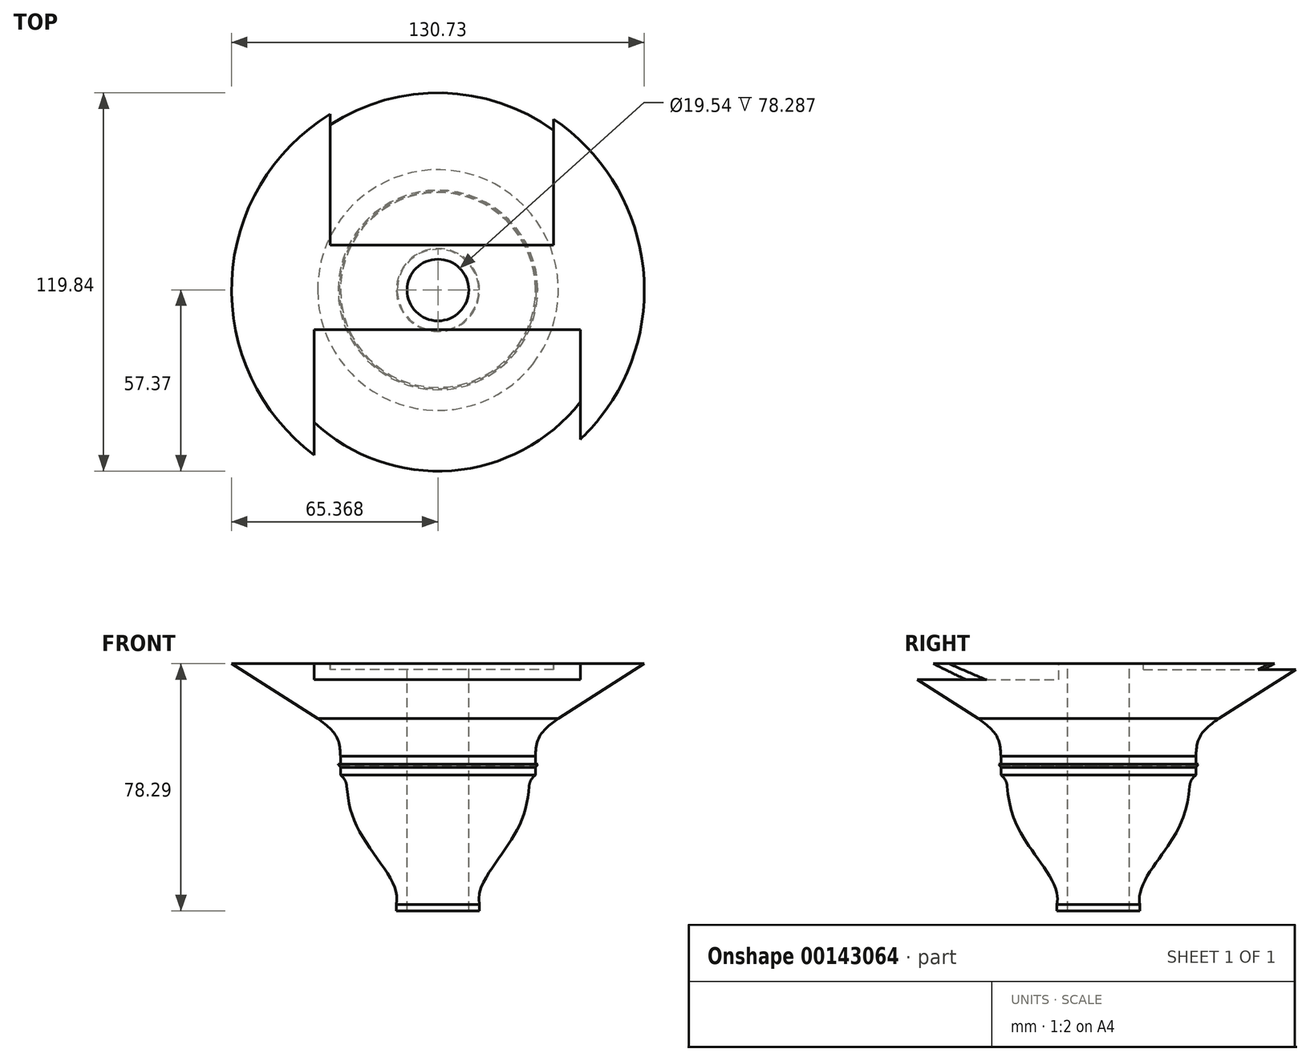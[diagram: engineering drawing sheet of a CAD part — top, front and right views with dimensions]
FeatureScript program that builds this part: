
annotation { "Feature Type Name" : "Feature", "Feature Type Description" : "" }
export const myFeature = defineFeature(function(context is Context, id is Id, definition is map)
    precondition{}
    {
        {
            var Q0;
            Q0=qCreatedBy(makeId("Front.planeOp"),FACE);
            var sketch = newSketch(context, id + "F0", { "sketchPlane" : qUnion([Q0])});
            skFitSpline(sketch, "E0", {"points": [v(-16.1, 126.64) * mm, v(-18.84, 136.35) * mm, v(-29, 152.21) * mm, v(-32.04, 167.7) * mm], "startDerivative": vector(7.14, 34.5) * mm, "endDerivative": vector(-1.92, 45.42) * mm});
            skLineSegment(sketch, "E1", {"start": v(-16.1, 126.64) * mm, "end": v(-16.1, 124.66) * mm});
            skLineSegment(sketch, "E2", {"start": v(-10.62, 126.64) * mm, "end": v(-10.62, 167.95) * mm});
            skLineSegment(sketch, "E3", {"start": v(-2.94, 126.64) * mm, "end": v(-2.94, 174.6) * mm});
            skLineSegment(sketch, "E4", {"start": v(-10.62, 167.95) * mm, "end": v(-10.62, 173.6) * mm});
            skLineSegment(sketch, "E5", {"start": v(-32.04, 167.7) * mm, "end": v(-33.8, 167.7) * mm});
            skLineSegment(sketch, "E6", {"start": v(-33.8, 170.13) * mm, "end": v(-34.56, 171.1) * mm});
            skLineSegment(sketch, "E7", {"start": v(-34.56, 171.1) * mm, "end": v(-34.18, 171.1) * mm});
            skLineSegment(sketch, "E8", {"start": v(-34.18, 171.1) * mm, "end": v(-33.82, 170.66) * mm});
            skLineSegment(sketch, "E9", {"start": v(-33.8, 170.8) * mm, "end": v(-34.18, 171.27) * mm});
            skLineSegment(sketch, "E10", {"start": v(-34.18, 171.27) * mm, "end": v(-34.6, 171.27) * mm});
            skLineSegment(sketch, "E11", {"start": v(-34.6, 171.27) * mm, "end": v(-33.8, 170.24) * mm});
            skLineSegment(sketch, "E12", {"start": v(-33.82, 170.66) * mm, "end": v(-33.82, 173.6) * mm});
            skLineSegment(sketch, "E13", {"start": v(-33.8, 170.13) * mm, "end": v(-33.8, 167.7) * mm});
            skLineSegment(sketch, "E14", {"start": v(-10.62, 124.66) * mm, "end": v(-10.62, 126.64) * mm});
            skLineSegment(sketch, "E15", {"start": v(-16.1, 124.66) * mm, "end": v(-10.62, 124.66) * mm});
            skFitSpline(sketch, "E16", {"points": [v(-33.82, 173.6) * mm, v(-35.08, 179.84) * mm, v(-41.06, 185.63) * mm], "startDerivative": vector(-0.72, 13.96) * mm, "endDerivative": vector(-13.48, 10.18) * mm});
            skLineSegment(sketch, "E17", {"start": v(-10.62, 173.6) * mm, "end": v(-10.62, 192.7) * mm});
            skLineSegment(sketch, "E18", {"start": v(-41.06, 185.63) * mm, "end": v(-56.9, 195.7) * mm});
            skLineSegment(sketch, "E19", {"start": v(-56.9, 195.7) * mm, "end": v(-68.3, 202.95) * mm});
            skLineSegment(sketch, "E20", {"start": v(-68.3, 202.95) * mm, "end": v(-10.62, 202.95) * mm});
            skLineSegment(sketch, "E21", {"start": v(-10.62, 202.95) * mm, "end": v(-10.62, 192.7) * mm});
            skSolve(sketch);
        }
        {
            var Q0;
            Q0=makeQuery(id+"F0.imprint","IMPRINT",FACE,{"disambiguationData":[TD([[makeQuery(id+"F0.imprint","IMPRINT",EDGE,{"derivedFrom":sQuery(id+"F0.wireOp",EDGE,"E0")}),-1.0]])]});
            var Q1;
            Q1=sQuery(id+"F0.wireOp",EDGE,"E3");
            revolve(context, id + "F1", {"entities" : qUnion([Q0]), "axis" : qUnion([Q1]), "revolveType" : RevolveType.FULL});
        }
        {
            var Q0;
            Q0=makeQuery(id+"F1.opRevolve","SWEPT_EDGE",EDGE,{"disambiguationData":[OSD([sQuery(id+"F0.wireOp",EDGE,"E0"),sQuery(id+"F0.wireOp",EDGE,"E5")])]});
            fillet(context, id + "F2", {"entities" : qUnion([Q0]), "radius" : 5.08 * mm, "tangentPropagation" : true, "allowEdgeOverflow" : false});
        }
        {
            var Q0;
            Q0=makeQuery(id+"F1.opRevolve","SWEPT_FACE",FACE,{"disambiguationData":[OSD([sQuery(id+"F0.wireOp",EDGE,"E20")])]});
            var sketch = newSketch(context, id + "F3", { "sketchPlane" : qUnion([Q0])});
            skCircle(sketch, "E22", {"center": v(-2.94, 0) * mm, "radius": 9.77 * mm});
            skLineSegment(sketch, "E23.bottom", {"start": v(33.7, 14.2) * mm, "end": v(-37.09, 14.2) * mm});
            skLineSegment(sketch, "E23.top", {"start": v(33.7, 67.54) * mm, "end": v(-37.09, 67.54) * mm});
            skLineSegment(sketch, "E23.left", {"start": v(33.7, 14.2) * mm, "end": v(33.7, 67.54) * mm});
            skLineSegment(sketch, "E23.right", {"start": v(-37.09, 14.2) * mm, "end": v(-37.09, 67.54) * mm});
            skPoint(sketch, "E23.middle", {"position": v(-1.7, 40.87) * mm});
            skLineSegment(sketch, "E24.bottom", {"start": v(-42.16, -69.14) * mm, "end": v(42.16, -69.14) * mm});
            skLineSegment(sketch, "E24.top", {"start": v(-42.16, -12.5) * mm, "end": v(42.16, -12.5) * mm});
            skLineSegment(sketch, "E24.left", {"start": v(-42.16, -69.14) * mm, "end": v(-42.16, -12.5) * mm});
            skLineSegment(sketch, "E24.right", {"start": v(42.16, -69.14) * mm, "end": v(42.16, -12.5) * mm});
            skPoint(sketch, "E24.middle", {"position": v(0, -40.82) * mm});
            skSolve(sketch);
        }
        {
            var Q0;
            Q0=makeQuery(id+"F3.imprint","IMPRINT",FACE,{"disambiguationData":[TD([[makeQuery(id+"F3.imprint","IMPRINT",EDGE,{"derivedFrom":sQuery(id+"F3.wireOp",EDGE,"E22")}),1.0]])]});
            extrude(context, id + "F4", {"entities" : qUnion([Q0]), "operationType" : NewBodyOperationType.REMOVE, "oppositeDirection" : true, "depth" : 86.26 * mm});
        }
        {
            var Q0;
            {var subQ0=sQuery(id+"F3.wireOp",EDGE,"E23.bottom");Q0=makeQuery(id+"F3.imprint","IMPRINT",FACE,{"disambiguationData":[TD([[makeQuery(id+"F3.imprint","IMPRINT",EDGE,{"derivedFrom":subQ0}),-1.0]])]});}
            extrude(context, id + "F5", {"entities" : qUnion([Q0]), "operationType" : NewBodyOperationType.REMOVE, "oppositeDirection" : true, "depth" : 1.84 * mm});
        }
        {
            var Q0;
            {var subQ0=sQuery(id+"F3.wireOp",EDGE,"E24.top");Q0=makeQuery(id+"F3.imprint","IMPRINT",FACE,{"disambiguationData":[TD([[makeQuery(id+"F3.imprint","IMPRINT",EDGE,{"derivedFrom":subQ0}),-1.0]])]});}
            extrude(context, id + "F6", {"entities" : qUnion([Q0]), "operationType" : NewBodyOperationType.REMOVE, "oppositeDirection" : true, "depth" : 5.08 * mm});
        }
    });
